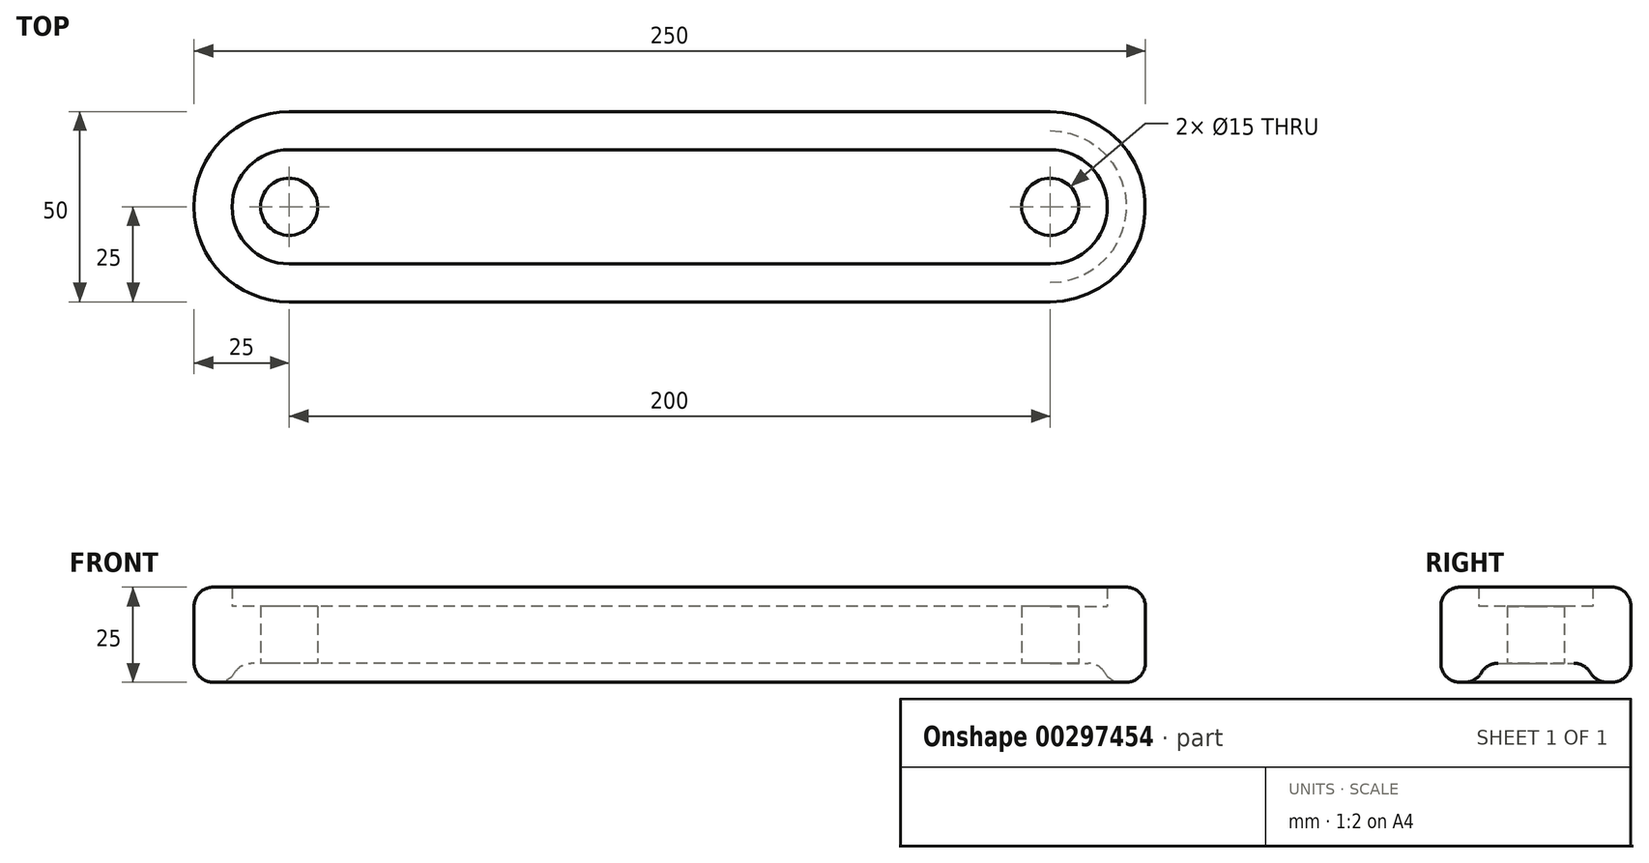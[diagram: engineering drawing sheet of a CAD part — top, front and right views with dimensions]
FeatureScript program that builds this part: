
annotation { "Feature Type Name" : "Feature", "Feature Type Description" : "" }
export const myFeature = defineFeature(function(context is Context, id is Id, definition is map)
    precondition{}
    {
        {
            var Q0;
            Q0=qCreatedBy(makeId("Top.planeOp"),FACE);
            var sketch = newSketch(context, id + "F0", { "sketchPlane" : qUnion([Q0])});
            skLineSegment(sketch, "E0.bottom", {"start": v(100, 15) * mm, "end": v(-100, 15) * mm});
            skLineSegment(sketch, "E0.top", {"start": v(100, -15) * mm, "end": v(-100, -15) * mm});
            skPoint(sketch, "E0.middle", {"position": v(0, 0) * mm});
            skLineSegment(sketch, "E1.bottom", {"start": v(100, 25) * mm, "end": v(-100, 25) * mm});
            skLineSegment(sketch, "E1.top", {"start": v(100, -25) * mm, "end": v(-100, -25) * mm});
            skArc(sketch, "E2", {"start": v(-100, -25) * mm, "mid": v(-125, 0) * mm, "end": v(-100, 25) * mm});
            skArc(sketch, "E3", {"start": v(100, -25) * mm, "mid": v(125, 0) * mm, "end": v(100, 25) * mm});
            skCircle(sketch, "E4", {"center": v(-100, 0) * mm, "radius": 15 * mm});
            skCircle(sketch, "E5", {"center": v(100, 0) * mm, "radius": 15 * mm});
            skCircle(sketch, "E6", {"center": v(-100, 0) * mm, "radius": 7.5 * mm});
            skCircle(sketch, "E7", {"center": v(100, 0) * mm, "radius": 7.5 * mm});
            skSolve(sketch);
        }
        {
            var Q0;
            {var subQ1=sQuery(id+"F0.wireOp",EDGE,"E0.bottom");Q0=makeQuery(id+"F0.imprint","IMPRINT",FACE,{"disambiguationData":[TD([[makeQuery(id+"F0.imprint","IMPRINT",EDGE,{"derivedFrom":subQ1}),-1.0]])]});}
            extrude(context, id + "F1", {"entities" : qUnion([Q0]), "endBound" : BoundingType.SYMMETRIC, "depth" : 25 * mm});
        }
        {
            var Q0;
            {var subQ0=sQuery(id+"F0.wireOp",EDGE,"E5");var subQ1=makeQuery(id+"F0.imprint","INTERSECT",VERTEX,{"derivedFrom":[sQuery(id+"F0.wireOp",EDGE,"E0.bottom"),subQ0]});Q0=makeQuery(id+"F0.imprint","IMPRINT",FACE,{"disambiguationData":[TD([[makeQuery(id+"F0.imprint","IMPRINT",EDGE,{"disambiguationData":[TD([[subQ1,-1.0]])],"derivedFrom":subQ0}),1.0]])]});}
            var Q1;
            {var subQ0=sQuery(id+"F0.wireOp",EDGE,"E0.bottom");Q1=makeQuery(id+"F0.imprint","IMPRINT",FACE,{"disambiguationData":[TD([[makeQuery(id+"F0.imprint","IMPRINT",EDGE,{"derivedFrom":subQ0}),1.0]])]});}
            var Q2;
            {var subQ0=sQuery(id+"F0.wireOp",EDGE,"E4");var subQ1=makeQuery(id+"F0.imprint","INTERSECT",VERTEX,{"derivedFrom":[sQuery(id+"F0.wireOp",EDGE,"E0.bottom"),subQ0]});Q2=makeQuery(id+"F0.imprint","IMPRINT",FACE,{"disambiguationData":[TD([[makeQuery(id+"F0.imprint","IMPRINT",EDGE,{"disambiguationData":[TD([[subQ1,-1.0]])],"derivedFrom":subQ0}),1.0]])]});}
            extrude(context, id + "F2", {"entities" : qUnion([Q0, Q1, Q2]), "operationType" : NewBodyOperationType.ADD, "endBound" : BoundingType.SYMMETRIC, "depth" : 15 * mm});
        }
        {
            var Q0;
            Q0=makeQuery(id+"F2.opExtrude","CAP_EDGE",EDGE,{"disambiguationData":[OSD([sQuery(id+"F0.wireOp",EDGE,"E0.top")])],"isStart":true});
            var Q1;
            Q1=makeQuery(id+"F2.opExtrude","CAP_EDGE",EDGE,{"disambiguationData":[OSD([sQuery(id+"F0.wireOp",EDGE,"E0.bottom")])],"isStart":true});
            var Q2;
            Q2=makeQuery(id+"F2.opExtrude","CAP_EDGE",EDGE,{"disambiguationData":[OSD([sQuery(id+"F0.wireOp",EDGE,"E0.bottom")])],"isStart":false});
            var Q3;
            Q3=makeQuery(id+"F1.opExtrude","CAP_EDGE",EDGE,{"disambiguationData":[OSD([sQuery(id+"F0.wireOp",EDGE,"E2")])],"isStart":true});
            var Q4;
            Q4=makeQuery(id+"F1.opExtrude","CAP_EDGE",EDGE,{"disambiguationData":[OSD([sQuery(id+"F0.wireOp",EDGE,"E2")])],"isStart":false});
            fillet(context, id + "F3", {"entities" : qUnion([Q0, Q1, Q2, Q3, Q4]), "radius" : 5 * mm, "tangentPropagation" : true, "allowEdgeOverflow" : false});
        }
        {
            var Q0;
            {var subQ0=sQuery(id+"F0.wireOp",EDGE,"E0.bottom");Q0=makeQuery(id+"F3.opFillet","BLEND_EDGE",EDGE,{"blendedFrom":[makeQuery(id+"F2.opExtrude","CAP_EDGE",EDGE,{"disambiguationData":[OSD([subQ0])],"isStart":false}),makeQuery(id+"F1.opExtrude","CAP_FACE",FACE,{"disambiguationData":[OSD([subQ0,sQuery(id+"F0.wireOp",EDGE,"E0.top"),sQuery(id+"F0.wireOp",EDGE,"E1.bottom"),sQuery(id+"F0.wireOp",EDGE,"E1.top"),sQuery(id+"F0.wireOp",EDGE,"E2"),sQuery(id+"F0.wireOp",EDGE,"E3"),sQuery(id+"F0.wireOp",EDGE,"E4"),sQuery(id+"F0.wireOp",EDGE,"E5")])],"isStart":false})],"blendedInto":[makeQuery(id+"F1.opExtrude","CAP_FACE",FACE,{"disambiguationData":[OSD([subQ0,sQuery(id+"F0.wireOp",EDGE,"E0.top"),sQuery(id+"F0.wireOp",EDGE,"E1.bottom"),sQuery(id+"F0.wireOp",EDGE,"E1.top"),sQuery(id+"F0.wireOp",EDGE,"E2"),sQuery(id+"F0.wireOp",EDGE,"E3"),sQuery(id+"F0.wireOp",EDGE,"E4"),sQuery(id+"F0.wireOp",EDGE,"E5")])],"isStart":false})]});}
            var Q1;
            {var subQ0=sQuery(id+"F0.wireOp",EDGE,"E0.bottom");Q1=makeQuery(id+"F3.opFillet","BLEND_EDGE",EDGE,{"blendedFrom":[makeQuery(id+"F2.opExtrude","CAP_EDGE",EDGE,{"disambiguationData":[OSD([subQ0])],"isStart":true}),makeQuery(id+"F1.opExtrude","CAP_FACE",FACE,{"disambiguationData":[OSD([subQ0,sQuery(id+"F0.wireOp",EDGE,"E0.top"),sQuery(id+"F0.wireOp",EDGE,"E1.bottom"),sQuery(id+"F0.wireOp",EDGE,"E1.top"),sQuery(id+"F0.wireOp",EDGE,"E2"),sQuery(id+"F0.wireOp",EDGE,"E3"),sQuery(id+"F0.wireOp",EDGE,"E4"),sQuery(id+"F0.wireOp",EDGE,"E5")])],"isStart":true})],"blendedInto":[makeQuery(id+"F1.opExtrude","CAP_FACE",FACE,{"disambiguationData":[OSD([subQ0,sQuery(id+"F0.wireOp",EDGE,"E0.top"),sQuery(id+"F0.wireOp",EDGE,"E1.bottom"),sQuery(id+"F0.wireOp",EDGE,"E1.top"),sQuery(id+"F0.wireOp",EDGE,"E2"),sQuery(id+"F0.wireOp",EDGE,"E3"),sQuery(id+"F0.wireOp",EDGE,"E4"),sQuery(id+"F0.wireOp",EDGE,"E5")])],"isStart":true})]});}
            fillet(context, id + "F4", {"entities" : qUnion([Q0, Q1]), "radius" : 5 * mm, "tangentPropagation" : true, "allowEdgeOverflow" : false});
        }
    });
